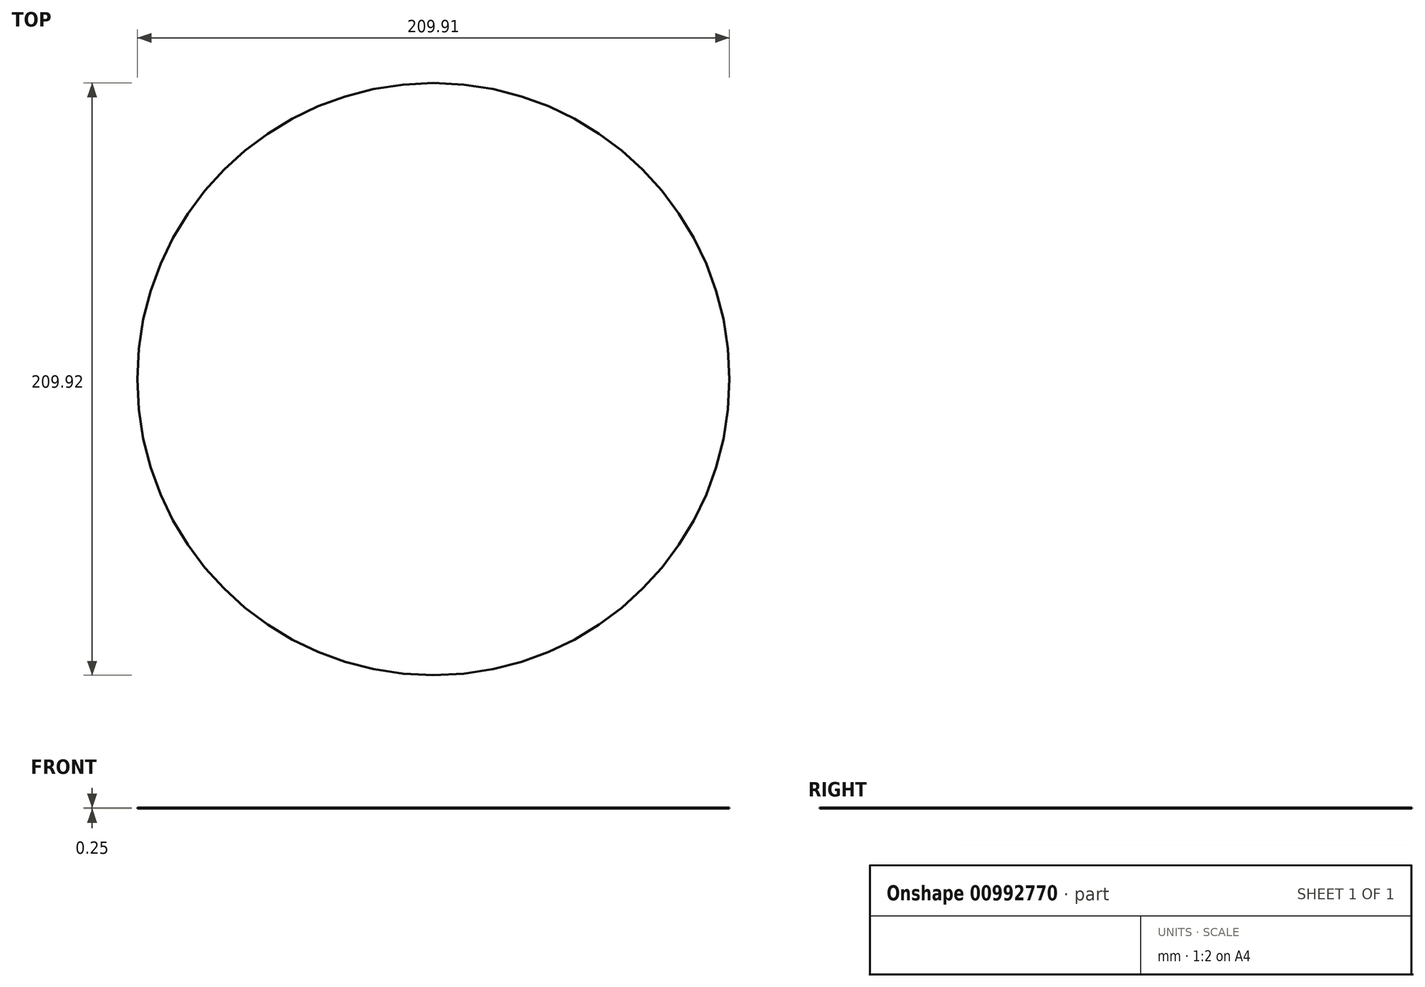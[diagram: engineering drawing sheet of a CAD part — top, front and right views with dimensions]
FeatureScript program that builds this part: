
annotation { "Feature Type Name" : "Feature", "Feature Type Description" : "" }
export const myFeature = defineFeature(function(context is Context, id is Id, definition is map)
    precondition{}
    {
        {
            var Q0;
            Q0=qCreatedBy(makeId("Top.planeOp"),FACE);
            var sketch = newSketch(context, id + "F0", { "sketchPlane" : qUnion([Q0])});
            skCircle(sketch, "E0", {"center": v(-11, 0) * mm, "radius": 104.96 * mm});
            skSolve(sketch);
        }
        {
            var Q0;
            Q0=makeQuery(id+"F0.imprint","IMPRINT",FACE,{"disambiguationData":[TD([[makeQuery(id+"F0.imprint","IMPRINT",EDGE,{"derivedFrom":sQuery(id+"F0.wireOp",EDGE,"E0")}),1.0]])]});
            extrude(context, id + "F1", {"entities" : qUnion([Q0]), "depth" : 0.25 * mm, "offsetDistance" : 25.4 * mm});
        }
    });
